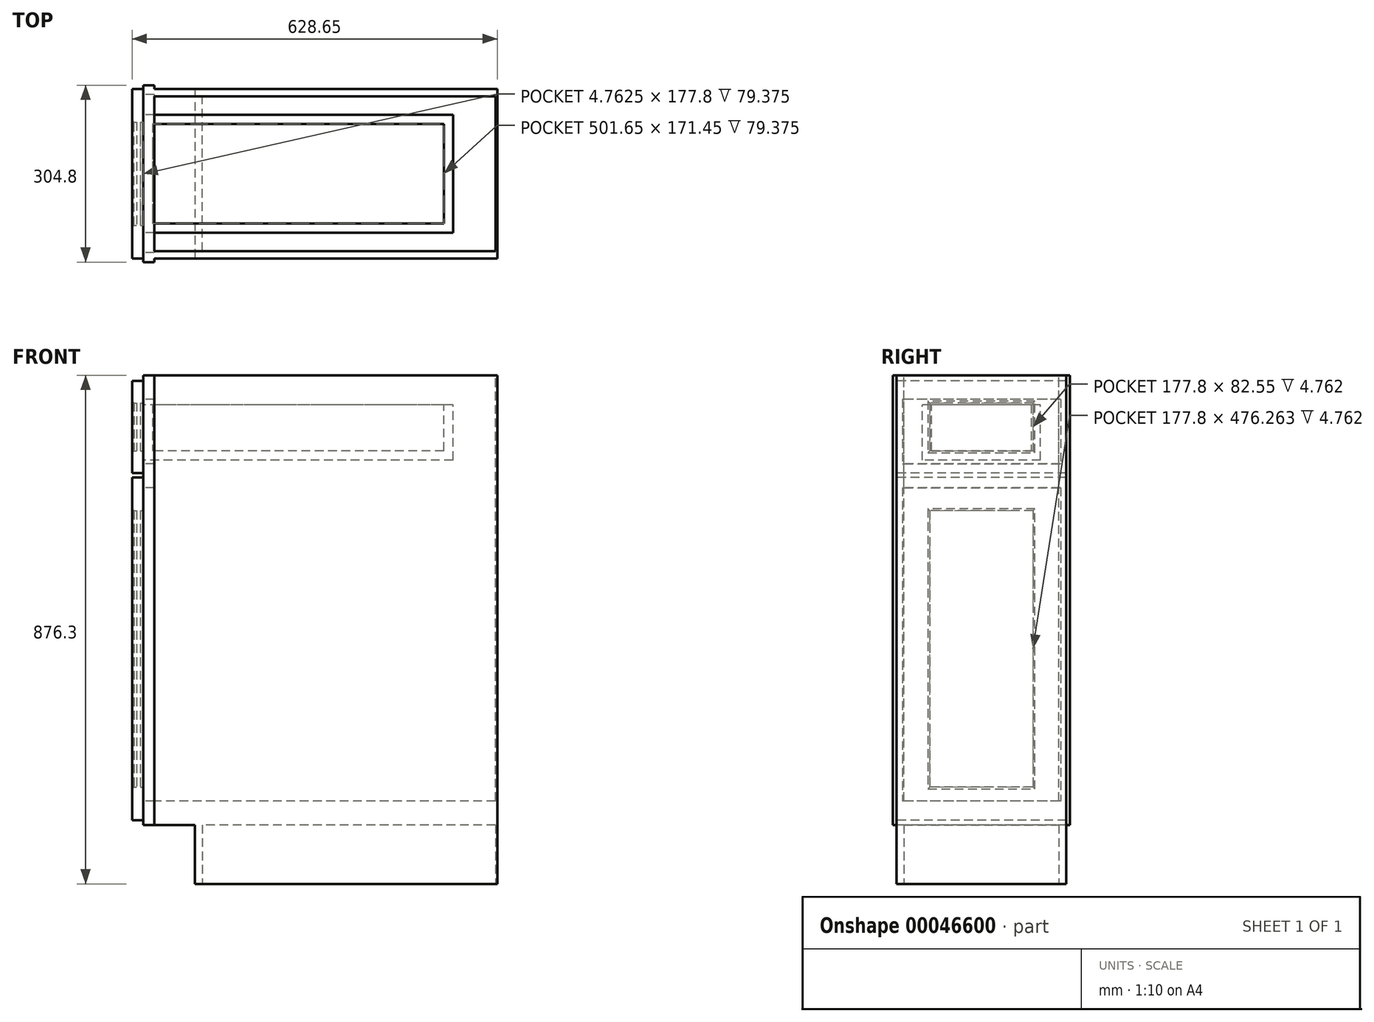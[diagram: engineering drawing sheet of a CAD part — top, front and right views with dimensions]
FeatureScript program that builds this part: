
annotation { "Feature Type Name" : "Feature", "Feature Type Description" : "" }
export const myFeature = defineFeature(function(context is Context, id is Id, definition is map)
    precondition{}
    {
        {
            var Q0;
            Q0=qCreatedBy(makeId("Front.planeOp"),FACE);
            var sketch = newSketch(context, id + "F0", { "sketchPlane" : qUnion([Q0])});
            skLineSegment(sketch, "E0.bottom", {"start": v(-304.8, -438.15) * mm, "end": v(304.8, -438.15) * mm});
            skLineSegment(sketch, "E0.top", {"start": v(-304.8, 438.15) * mm, "end": v(304.8, 438.15) * mm});
            skLineSegment(sketch, "E0.left", {"start": v(-304.8, -438.15) * mm, "end": v(-304.8, 438.15) * mm});
            skLineSegment(sketch, "E0.right", {"start": v(304.8, -438.15) * mm, "end": v(304.8, 438.15) * mm});
            skLineSegment(sketch, "E1", {"start": v(-304.8, -438.15) * mm, "end": v(304.8, 438.15) * mm, "construction": true});
            skSolve(sketch);
        }
        {
            var Q0;
            Q0=qSketchRegion(id+"F0",true);
            extrude(context, id + "F1", {"entities" : qUnion([Q0]), "oppositeDirection" : true, "depth" : 304.8 * mm});
        }
        {
            var Q0;
            Q0=makeQuery(id+"F1.opExtrude","CAP_FACE",FACE,{"disambiguationData":[OSD([sQuery(id+"F0.wireOp",EDGE,"E0.bottom"),sQuery(id+"F0.wireOp",EDGE,"E0.top"),sQuery(id+"F0.wireOp",EDGE,"E0.left"),sQuery(id+"F0.wireOp",EDGE,"E0.right")])],"isStart":true});
            var sketch = newSketch(context, id + "F2", { "sketchPlane" : qUnion([Q0])});
            skLineSegment(sketch, "E2.bottom", {"start": v(-304.8, -438.15) * mm, "end": v(-215.9, -438.15) * mm});
            skLineSegment(sketch, "E2.top", {"start": v(-304.8, -336.55) * mm, "end": v(-215.9, -336.55) * mm});
            skLineSegment(sketch, "E2.left", {"start": v(-304.8, -438.15) * mm, "end": v(-304.8, -336.55) * mm});
            skLineSegment(sketch, "E2.right", {"start": v(-215.9, -438.15) * mm, "end": v(-215.9, -336.55) * mm});
            skSolve(sketch);
        }
        {
            var Q0;
            Q0=qSketchRegion(id+"F2",true);
            extrude(context, id + "F3", {"entities" : qUnion([Q0]), "operationType" : NewBodyOperationType.REMOVE, "endBound" : BoundingType.THROUGH_ALL, "oppositeDirection" : true, "depth" : 25.4 * mm});
        }
        {
            var Q0;
            Q0=makeQuery(id+"F1.opExtrude","SWEPT_FACE",FACE,{"disambiguationData":[OSD([sQuery(id+"F0.wireOp",EDGE,"E0.left")])]});
            var sketch = newSketch(context, id + "F4", { "sketchPlane" : qUnion([Q0])});
            skLineSegment(sketch, "E3.bottom", {"start": v(-288.56, 396.88) * mm, "end": v(-16.24, 396.88) * mm});
            skLineSegment(sketch, "E3.top", {"start": v(-288.56, -295.28) * mm, "end": v(-16.24, -295.28) * mm});
            skLineSegment(sketch, "E3.left", {"start": v(-288.56, 396.88) * mm, "end": v(-288.56, -295.28) * mm});
            skLineSegment(sketch, "E3.right", {"start": v(-16.24, 396.88) * mm, "end": v(-16.24, -295.28) * mm});
            skLineSegment(sketch, "E4", {"start": v(-304.8, 438.15) * mm, "end": v(0, -336.55) * mm, "construction": true});
            skSolve(sketch);
        }
        {
            var Q0;
            Q0=qSketchRegion(id+"F4",true);
            extrude(context, id + "F5", {"entities" : qUnion([Q0]), "operationType" : NewBodyOperationType.REMOVE, "oppositeDirection" : true, "depth" : 19.05 * mm});
        }
        {
            var Q0;
            Q0=makeQuery(id+"F1.opExtrude","SWEPT_FACE",FACE,{"disambiguationData":[OSD([sQuery(id+"F0.wireOp",EDGE,"E0.top")])]});
            var sketch = newSketch(context, id + "F6", { "sketchPlane" : qUnion([Q0])});
            skLineSegment(sketch, "E5.bottom", {"start": v(304.8, 304.8) * mm, "end": v(-285.75, 304.8) * mm});
            skLineSegment(sketch, "E5.top", {"start": v(304.8, 298.45) * mm, "end": v(-285.75, 298.45) * mm});
            skLineSegment(sketch, "E5.left", {"start": v(304.8, 304.8) * mm, "end": v(304.8, 298.45) * mm});
            skLineSegment(sketch, "E5.right", {"start": v(-285.75, 304.8) * mm, "end": v(-285.75, 298.45) * mm});
            skLineSegment(sketch, "E6.bottom", {"start": v(304.8, 0) * mm, "end": v(-285.75, 0) * mm});
            skLineSegment(sketch, "E6.top", {"start": v(304.8, 6.35) * mm, "end": v(-285.75, 6.35) * mm});
            skLineSegment(sketch, "E6.left", {"start": v(304.8, 0) * mm, "end": v(304.8, 6.35) * mm});
            skLineSegment(sketch, "E6.right", {"start": v(-285.75, 0) * mm, "end": v(-285.75, 6.35) * mm});
            skSolve(sketch);
        }
        {
            var Q0;
            Q0=qSketchRegion(id+"F6",true);
            extrude(context, id + "F7", {"entities" : qUnion([Q0]), "operationType" : NewBodyOperationType.REMOVE, "endBound" : BoundingType.THROUGH_ALL, "oppositeDirection" : true, "depth" : 25.4 * mm});
        }
        {
            var Q0;
            Q0=makeQuery(id+"F1.opExtrude","SWEPT_FACE",FACE,{"disambiguationData":[OSD([sQuery(id+"F0.wireOp",EDGE,"E0.top")])]});
            var sketch = newSketch(context, id + "F8", { "sketchPlane" : qUnion([Q0])});
            skLineSegment(sketch, "E7.bottom", {"start": v(301.63, 285.75) * mm, "end": v(-285.75, 285.75) * mm});
            skLineSegment(sketch, "E7.top", {"start": v(301.63, 19.05) * mm, "end": v(-285.75, 19.05) * mm});
            skLineSegment(sketch, "E7.left", {"start": v(301.63, 285.75) * mm, "end": v(301.63, 19.05) * mm});
            skLineSegment(sketch, "E7.right", {"start": v(-285.75, 285.75) * mm, "end": v(-285.75, 19.05) * mm});
            skSolve(sketch);
        }
        {
            var Q0;
            Q0=qSketchRegion(id+"F8",true);
            var Q1;
            Q1=makeQuery(id+"F5.boolean.opBoolean","COPY",FACE,{"derivedFrom":makeQuery(id+"F5.opExtrude","SWEPT_FACE",FACE,{"disambiguationData":[OSD([sQuery(id+"F4.wireOp",EDGE,"E3.top")])]})});
            extrude(context, id + "F9", {"entities" : qUnion([Q0]), "operationType" : NewBodyOperationType.REMOVE, "endBound" : BoundingType.UP_TO_SURFACE, "oppositeDirection" : true, "endBoundEntityFace" : qUnion([Q1]), "depth" : 25.4 * mm});
        }
        {
            var Q0;
            Q0=makeQuery(id+"F1.opExtrude","SWEPT_FACE",FACE,{"disambiguationData":[OSD([sQuery(id+"F0.wireOp",EDGE,"E0.left")])]});
            var sketch = newSketch(context, id + "F10", { "sketchPlane" : qUnion([Q0])});
            skLineSegment(sketch, "E8.bottom", {"start": v(-288.56, 285.75) * mm, "end": v(-16.24, 285.75) * mm});
            skLineSegment(sketch, "E8.top", {"start": v(-288.56, 244.47) * mm, "end": v(-16.24, 244.47) * mm});
            skLineSegment(sketch, "E8.left", {"start": v(-288.56, 285.75) * mm, "end": v(-288.56, 244.47) * mm});
            skLineSegment(sketch, "E8.right", {"start": v(-16.24, 285.75) * mm, "end": v(-16.24, 244.47) * mm});
            skSolve(sketch);
        }
        {
            var Q0;
            Q0=qSketchRegion(id+"F10",true);
            var Q1;
            Q1=makeQuery(id+"F9.boolean.opBoolean","COPY",FACE,{"derivedFrom":makeQuery(id+"F9.opExtrude","SWEPT_FACE",FACE,{"disambiguationData":[OSD([sQuery(id+"F8.wireOp",EDGE,"E7.right")])]})});
            extrude(context, id + "F11", {"entities" : qUnion([Q0]), "operationType" : NewBodyOperationType.ADD, "endBound" : BoundingType.UP_TO_SURFACE, "oppositeDirection" : true, "endBoundEntityFace" : qUnion([Q1]), "depth" : 25.4 * mm});
        }
        {
            var Q0;
            Q0=makeQuery(id+"F11.boolean.opBoolean","MERGE",FACE,{"derivedFrom":[makeQuery(id+"F1.opExtrude","SWEPT_FACE",FACE,{"disambiguationData":[OSD([sQuery(id+"F0.wireOp",EDGE,"E0.left")])]}),makeQuery(id+"F11.opExtrude","CAP_FACE",FACE,{"disambiguationData":[OSD([sQuery(id+"F10.wireOp",EDGE,"E8.bottom"),sQuery(id+"F10.wireOp",EDGE,"E8.top"),sQuery(id+"F10.wireOp",EDGE,"E8.left"),sQuery(id+"F10.wireOp",EDGE,"E8.right")])],"isStart":true})]});
            var sketch = newSketch(context, id + "F12", { "sketchPlane" : qUnion([Q0])});
            skLineSegment(sketch, "E9.bottom", {"start": v(-298.45, 261.95) * mm, "end": v(-6.35, 261.95) * mm});
            skLineSegment(sketch, "E9.top", {"start": v(-298.45, -328.61) * mm, "end": v(-6.35, -328.61) * mm});
            skLineSegment(sketch, "E9.left", {"start": v(-298.45, 261.95) * mm, "end": v(-298.45, -328.61) * mm});
            skLineSegment(sketch, "E9.right", {"start": v(-6.35, 261.95) * mm, "end": v(-6.35, -328.61) * mm});
            skLineSegment(sketch, "E10.bottom", {"start": v(-241.3, 204.8) * mm, "end": v(-63.5, 204.8) * mm});
            skLineSegment(sketch, "E10.top", {"start": v(-241.3, -271.46) * mm, "end": v(-63.5, -271.46) * mm});
            skLineSegment(sketch, "E10.left", {"start": v(-241.3, 204.8) * mm, "end": v(-241.3, -271.46) * mm});
            skLineSegment(sketch, "E10.right", {"start": v(-63.5, 204.8) * mm, "end": v(-63.5, -271.46) * mm});
            skSolve(sketch);
        }
        {
            var Q0;
            Q0=qSketchRegion(id+"F12",true);
            extrude(context, id + "F13", {"entities" : qUnion([Q0]), "depth" : 19.05 * mm});
        }
        {
            var Q0;
            Q0=makeQuery(id+"F13.opExtrude","SWEPT_FACE",FACE,{"disambiguationData":[OSD([sQuery(id+"F12.wireOp",EDGE,"E10.top")])]});
            var sketch = newSketch(context, id + "F14", { "sketchPlane" : qUnion([Q0])});
            skLineSegment(sketch, "E11.bottom", {"start": v(-315.91, 241.3) * mm, "end": v(-309.56, 241.3) * mm});
            skLineSegment(sketch, "E11.top", {"start": v(-315.91, 63.5) * mm, "end": v(-309.56, 63.5) * mm});
            skLineSegment(sketch, "E11.left", {"start": v(-315.91, 241.3) * mm, "end": v(-315.91, 63.5) * mm});
            skLineSegment(sketch, "E11.right", {"start": v(-309.56, 241.3) * mm, "end": v(-309.56, 63.5) * mm});
            skSolve(sketch);
        }
        {
            var Q0;
            Q0=qSketchRegion(id+"F14",true);
            extrude(context, id + "F15", {"entities" : qUnion([Q0]), "operationType" : NewBodyOperationType.ADD, "endBound" : BoundingType.UP_TO_NEXT, "depth" : 25.4 * mm});
        }
        {
            var Q0;
            Q0=makeQuery(id+"F13.opExtrude","CAP_EDGE",EDGE,{"disambiguationData":[OSD([sQuery(id+"F12.wireOp",EDGE,"E10.left")])],"isStart":false});
            var Q1;
            Q1=makeQuery(id+"F13.opExtrude","CAP_EDGE",EDGE,{"disambiguationData":[OSD([sQuery(id+"F12.wireOp",EDGE,"E10.top")])],"isStart":false});
            var Q2;
            Q2=makeQuery(id+"F13.opExtrude","CAP_EDGE",EDGE,{"disambiguationData":[OSD([sQuery(id+"F12.wireOp",EDGE,"E10.right")])],"isStart":false});
            var Q3;
            Q3=makeQuery(id+"F13.opExtrude","CAP_EDGE",EDGE,{"disambiguationData":[OSD([sQuery(id+"F12.wireOp",EDGE,"E10.bottom")])],"isStart":false});
            chamfer(context, id + "F16", {"entities" : qUnion([Q0, Q1, Q2, Q3]), "width" : 3.17 * mm, "tangentPropagation" : true});
        }
        {
            var Q0;
            Q0=makeQuery(id+"F11.boolean.opBoolean","MERGE",FACE,{"derivedFrom":[makeQuery(id+"F1.opExtrude","SWEPT_FACE",FACE,{"disambiguationData":[OSD([sQuery(id+"F0.wireOp",EDGE,"E0.left")])]}),makeQuery(id+"F11.opExtrude","CAP_FACE",FACE,{"disambiguationData":[OSD([sQuery(id+"F10.wireOp",EDGE,"E8.bottom"),sQuery(id+"F10.wireOp",EDGE,"E8.top"),sQuery(id+"F10.wireOp",EDGE,"E8.left"),sQuery(id+"F10.wireOp",EDGE,"E8.right")])],"isStart":true})]});
            var sketch = newSketch(context, id + "F17", { "sketchPlane" : qUnion([Q0])});
            skLineSegment(sketch, "E12.bottom", {"start": v(-298.45, 428.62) * mm, "end": v(-6.35, 428.62) * mm});
            skLineSegment(sketch, "E12.top", {"start": v(-298.45, 269.88) * mm, "end": v(-6.35, 269.88) * mm});
            skLineSegment(sketch, "E12.left", {"start": v(-298.45, 428.62) * mm, "end": v(-298.45, 269.88) * mm});
            skLineSegment(sketch, "E12.right", {"start": v(-6.35, 428.62) * mm, "end": v(-6.35, 269.88) * mm});
            skLineSegment(sketch, "E13.bottom", {"start": v(-241.3, 390.52) * mm, "end": v(-63.5, 390.52) * mm});
            skLineSegment(sketch, "E13.top", {"start": v(-241.3, 307.98) * mm, "end": v(-63.5, 307.98) * mm});
            skLineSegment(sketch, "E13.left", {"start": v(-241.3, 390.52) * mm, "end": v(-241.3, 307.98) * mm});
            skLineSegment(sketch, "E13.right", {"start": v(-63.5, 390.52) * mm, "end": v(-63.5, 307.98) * mm});
            skSolve(sketch);
        }
        {
            var Q0;
            Q0=qSketchRegion(id+"F17",true);
            extrude(context, id + "F18", {"entities" : qUnion([Q0]), "depth" : 19.05 * mm});
        }
        {
            var Q0;
            Q0=makeQuery(id+"F18.opExtrude","SWEPT_FACE",FACE,{"disambiguationData":[OSD([sQuery(id+"F17.wireOp",EDGE,"E13.top")])]});
            var sketch = newSketch(context, id + "F19", { "sketchPlane" : qUnion([Q0])});
            skLineSegment(sketch, "E14.bottom", {"start": v(-309.56, 241.3) * mm, "end": v(-315.91, 241.3) * mm});
            skLineSegment(sketch, "E14.top", {"start": v(-309.56, 63.5) * mm, "end": v(-315.91, 63.5) * mm});
            skLineSegment(sketch, "E14.left", {"start": v(-309.56, 241.3) * mm, "end": v(-309.56, 63.5) * mm});
            skLineSegment(sketch, "E14.right", {"start": v(-315.91, 241.3) * mm, "end": v(-315.91, 63.5) * mm});
            skSolve(sketch);
        }
        {
            var Q0;
            Q0=qSketchRegion(id+"F19",true);
            var Q1;
            Q1=makeQuery(id+"F18.opExtrude","SWEPT_FACE",FACE,{"disambiguationData":[OSD([sQuery(id+"F17.wireOp",EDGE,"E13.bottom")])]});
            extrude(context, id + "F20", {"entities" : qUnion([Q0]), "operationType" : NewBodyOperationType.ADD, "endBound" : BoundingType.UP_TO_SURFACE, "endBoundEntityFace" : qUnion([Q1]), "depth" : 25.4 * mm});
        }
        {
            var Q0;
            Q0=makeQuery(id+"F18.opExtrude","CAP_EDGE",EDGE,{"disambiguationData":[OSD([sQuery(id+"F17.wireOp",EDGE,"E13.top")])],"isStart":false});
            var Q1;
            Q1=makeQuery(id+"F18.opExtrude","CAP_EDGE",EDGE,{"disambiguationData":[OSD([sQuery(id+"F17.wireOp",EDGE,"E13.left")])],"isStart":false});
            var Q2;
            Q2=makeQuery(id+"F18.opExtrude","CAP_EDGE",EDGE,{"disambiguationData":[OSD([sQuery(id+"F17.wireOp",EDGE,"E13.bottom")])],"isStart":false});
            var Q3;
            Q3=makeQuery(id+"F18.opExtrude","CAP_EDGE",EDGE,{"disambiguationData":[OSD([sQuery(id+"F17.wireOp",EDGE,"E13.right")])],"isStart":false});
            chamfer(context, id + "F21", {"entities" : qUnion([Q0, Q1, Q2, Q3]), "width" : 3.17 * mm, "tangentPropagation" : true});
        }
        {
            var Q0;
            Q0=makeQuery(id+"F1.opExtrude","SWEPT_FACE",FACE,{"disambiguationData":[OSD([sQuery(id+"F0.wireOp",EDGE,"E0.bottom")])]});
            var sketch = newSketch(context, id + "F22", { "sketchPlane" : qUnion([Q0])});
            skLineSegment(sketch, "E15.bottom", {"start": v(301.63, -19.05) * mm, "end": v(-203.2, -19.05) * mm});
            skLineSegment(sketch, "E15.top", {"start": v(301.63, -285.75) * mm, "end": v(-203.2, -285.75) * mm});
            skLineSegment(sketch, "E15.left", {"start": v(301.63, -19.05) * mm, "end": v(301.63, -285.75) * mm});
            skLineSegment(sketch, "E15.right", {"start": v(-203.2, -19.05) * mm, "end": v(-203.2, -285.75) * mm});
            skSolve(sketch);
        }
        {
            var Q0;
            Q0=qSketchRegion(id+"F22",true);
            extrude(context, id + "F23", {"entities" : qUnion([Q0]), "operationType" : NewBodyOperationType.REMOVE, "oppositeDirection" : true, "depth" : 101.6 * mm});
        }
        {
            var Q0;
            Q0=makeQuery(id+"F18.opExtrude","CAP_FACE",FACE,{"disambiguationData":[OSD([sQuery(id+"F17.wireOp",EDGE,"E12.bottom"),sQuery(id+"F17.wireOp",EDGE,"E12.top"),sQuery(id+"F17.wireOp",EDGE,"E12.left"),sQuery(id+"F17.wireOp",EDGE,"E12.right"),sQuery(id+"F17.wireOp",EDGE,"E13.bottom"),sQuery(id+"F17.wireOp",EDGE,"E13.top"),sQuery(id+"F17.wireOp",EDGE,"E13.left"),sQuery(id+"F17.wireOp",EDGE,"E13.right")])],"isStart":true});
            var sketch = newSketch(context, id + "F24", { "sketchPlane" : qUnion([Q0])});
            skLineSegment(sketch, "E16.bottom", {"start": v(254, 292.1) * mm, "end": v(50.8, 292.1) * mm});
            skLineSegment(sketch, "E16.top", {"start": v(254, 387.35) * mm, "end": v(50.8, 387.35) * mm});
            skLineSegment(sketch, "E16.left", {"start": v(254, 292.1) * mm, "end": v(254, 387.35) * mm});
            skLineSegment(sketch, "E16.right", {"start": v(50.8, 292.1) * mm, "end": v(50.8, 387.35) * mm});
            skSolve(sketch);
        }
        {
            var Q0;
            Q0=qSketchRegion(id+"F24",true);
            extrude(context, id + "F25", {"entities" : qUnion([Q0]), "operationType" : NewBodyOperationType.ADD, "depth" : 533.4 * mm});
        }
        {
            var Q0;
            Q0=makeQuery(id+"F25.opExtrude","SWEPT_FACE",FACE,{"disambiguationData":[OSD([sQuery(id+"F24.wireOp",EDGE,"E16.top")])]});
            shell(context, id + "F26", {"entities" : qUnion([Q0]), "thickness" : 15.88 * mm});
        }
    });
